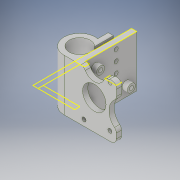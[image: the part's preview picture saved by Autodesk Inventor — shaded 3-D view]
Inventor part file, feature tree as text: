
AUTODESK INVENTOR PART (.ipt)
format: ipt  version: 2018 (Build 220112000, 112)  size: 216,064 bytes
history: native  units: in
note: dims shown in document units (in); Inventor stores cm internally (conversion verified against a paired STEP export)
features: sketch x8, other x3
ambient origin geometry x8: Origin, YZ Plane, XZ Plane, XY Plane, X Axis, Y Axis, Z Axis, Center Point
bodies: Solid1 (feature_tree)
feature tree (11):
  other  "motor mount 2.ipt"
  other  "Solid1::motor mount 2.ipt"
  other  "TaggingFeature1"
  sketch  "Sketch1"  dims[d0=0.3937in]
  sketch  "Sketch2"
  sketch  "Sketch4"
  sketch  "Sketch3"
  sketch  "Sketch5"
  sketch  "Sketch6"
  sketch  "Sketch7"
  sketch  "Sketch8"
